# Revit family: Bathtub-American_Standard-Town_Square_Suite-2742.068C.020
name_source: partatom
category: Plumbing Fixtures
units: mm (PartAtom-declared; Revit-internal decimal feet)

## family parameters
Always vertical = No
Cut with Voids When Loaded = No
OmniClass Number = 23.45.05.14.21
OmniClass Title = Bathtubs
Part Type = Normal
Room Calculation Point = No
Round Connector Dimension = Use Diameter
Shared = Yes
Work Plane-Based = Yes

## types (1)
- 2742068C.020
    Air Blower Remote Mounting Kit - 754025-0071 = Yes
    Assembly Code = D2010510
    B/S for Deck Mount Spout - 2555.652 (specify finish) = No
    B/S for Wall Mount Spout - 2555.602 (specify finish = No
    CW Connection = Yes
    CWFU = 3
    Compliance Certifications = Meets or Exceeds Underwriters Laboratories - Hydromassage,Bathtubs UL 1795, ASME A112.19.7M for Whirlpool Appliances, ANSI Z124.1 for Plastic Bathtubs, ASTM E162 for Flammability,NFPA 258 for Smoke Density
    D/M Filler less Personal Shower - 2555.90 (specify finish) = No
    D/M Filler with Personal Shower- 2555.901 (specify finish) = No
    Default Elevation = 0"
    Description = Town Square® 72 x 42-Inch Drop-In Bathtub With EverClean® Air Bath System
    Drain 1594.170 (specify finish) = Yes
    Drain Trim Kit 1585.200 (specify finish) = Yes
    Finish = Americast-American Standard-020-White
    Front Offset = 3 1/2"
    Gallon to Overflow = 69 gal. (261 l.)
    HW Connection = Yes
    HWFU = 3
    Height = 22"
    Installation Type = Floor Mounted
    Length = 71 1/2"
    Manufacturer = American Standard
    Material = Americast-American Standard-020-White
    Model = 2742068C.020
    Outlet Diameter = 1 1/2"
    Outlet Location = 13 1/4"
    Product Documentation Link = https://americanstandard.box.com
    Product Page URL = https://www.americanstandard-us.com
    Product Weight = 115 lbs. (52 kg.)
    Revised Date = 03/18/2021
    Type Comments = EverClean® Air Bath
    URL = https://www.americanstandard-us.com
    Vent Connection = No
    WFU = 4
    Warranty Information = Limited Lifetime Warranty
    Waste Connection = Yes
    Weight with Water/ Floor Loading = 690 lb. (313 kg)/33 lb./sq.ft. (161 kg/sq.m)
    Whirlpool Operating Volume = 60 gal. (227 l.)
    Width = 41 3/4"

## geometry (parser evidence)
native form markers: Sweep x2
no freeform markers — native parametric forms only
